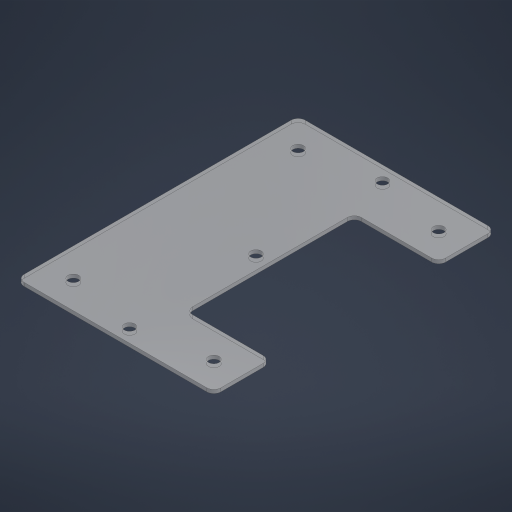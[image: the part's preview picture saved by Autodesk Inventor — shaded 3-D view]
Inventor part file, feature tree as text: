
AUTODESK INVENTOR PART (.ipt)
format: ipt  version: 2024 (Build 280153000, 153)  size: 221,184 bytes
history: native  units: in
note: dims shown in document units (in); Inventor stores cm internally (conversion verified against a paired STEP export)
features: sketch x1, extrude x1, hole x1
ambient origin geometry x8: Origin, YZ Plane, XZ Plane, XY Plane, X Axis, Y Axis, Z Axis, Center Point
bodies: Solid1 (feature_tree)
feature tree (3):
  sketch  "Sketch1"  dims[d0=3.5in d1=5.0in d2=1.0in d3=1.5in d4=1.0in d5=0.125in d6=0.0625in d7=0.0in d8=0.5in d10=2.5in d11=1.25in d12=0.25in d13=0.1875in d14=0.75in d15=0.375in d16=0.25in d17=0.5635in d18=1.0in d19=0.8108in]
  extrude  "Extrusion1"  Depth=5.0in
  hole  "Hole1"  [1 undecoded]
note: 1 required parameter value undecoded (feature->parameter linkage not recoverable at this tier; creation-order binding heuristic only, values carry confidence <= 0.55)
